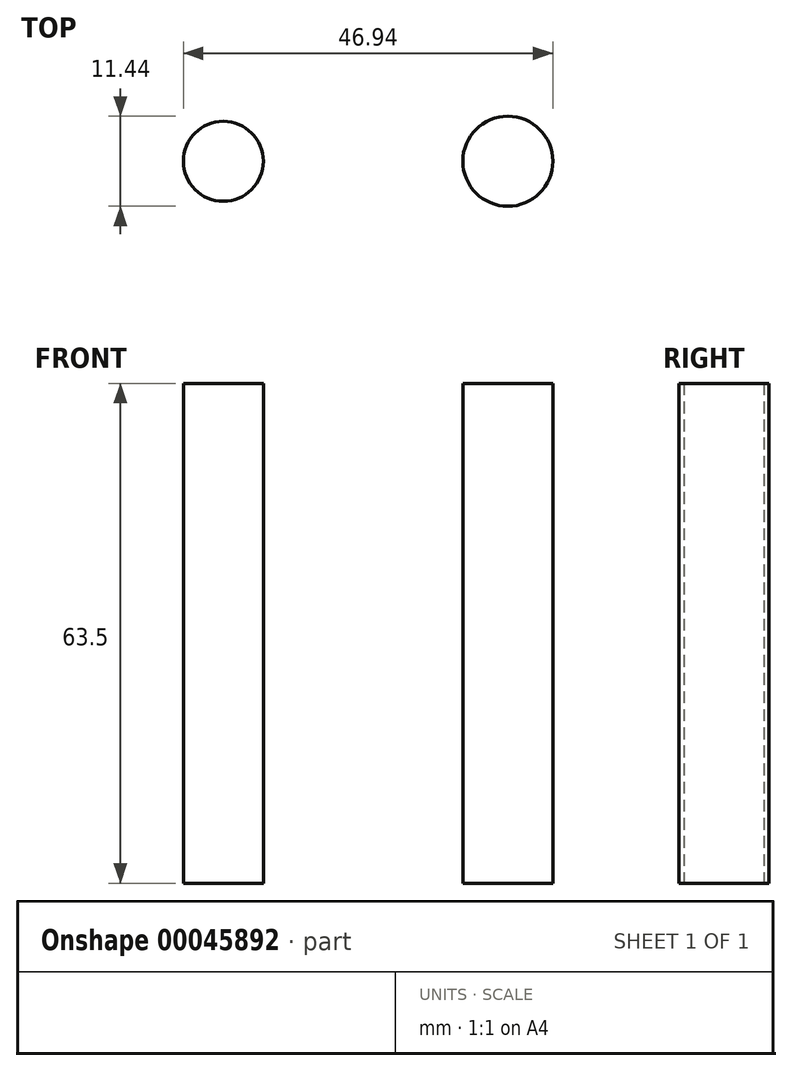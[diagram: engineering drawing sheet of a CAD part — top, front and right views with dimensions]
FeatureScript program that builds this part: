
annotation { "Feature Type Name" : "Feature", "Feature Type Description" : "" }
export const myFeature = defineFeature(function(context is Context, id is Id, definition is map)
    precondition{}
    {
        {
            var Q0;
            Q0=qCreatedBy(makeId("Top.planeOp"),FACE);
            var sketch = newSketch(context, id + "F0", { "sketchPlane" : qUnion([Q0])});
            skCircle(sketch, "E0", {"center": v(0, 0) * mm, "radius": 5.72 * mm});
            skCircle(sketch, "E1", {"center": v(-36.14, 0) * mm, "radius": 5.08 * mm});
            skSolve(sketch);
        }
        {
            var Q0;
            Q0=makeQuery(id+"F0.imprint","IMPRINT",FACE,{"disambiguationData":[TD([[makeQuery(id+"F0.imprint","IMPRINT",EDGE,{"derivedFrom":sQuery(id+"F0.wireOp",EDGE,"E0")}),1.0]])]});
            var Q1;
            Q1=makeQuery(id+"F0.imprint","IMPRINT",FACE,{"disambiguationData":[TD([[makeQuery(id+"F0.imprint","IMPRINT",EDGE,{"derivedFrom":sQuery(id+"F0.wireOp",EDGE,"E1")}),1.0]])]});
            extrude(context, id + "F1", {"entities" : qUnion([Q0, Q1]), "depth" : 63.5 * mm});
        }
    });
